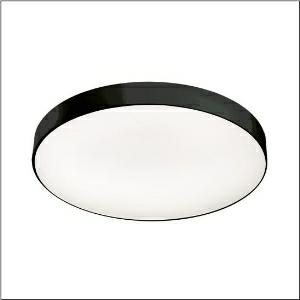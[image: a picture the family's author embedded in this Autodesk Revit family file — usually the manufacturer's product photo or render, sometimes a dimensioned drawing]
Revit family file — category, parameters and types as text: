
# Revit family: round_21_l_51mr38nd0421b
name_source: partatom
category: Lighting Fixtures
units: mm (PartAtom-declared; Revit-internal decimal feet)

## family parameters
Cut with Voids When Loaded = No
Host = Face
Light Source = No
Part Type = Normal
Room Calculation Point = No
Round Connector Dimension = Use Diameter
Shared = No

## types (1)
- Round 21 L (1 x LED, 12230 lm, 88.2 W, 4000K)
    Apparent Load = 88 VA
    CIE Flux Codes = 66 90 98 71 100
    Color Rendering = 80
    Color Temperature = 4000K
    Default Elevation = 1800 mm
    Description = Round 21 L, wall and ceiling luminaire, primary optical cover: micro prismatic cover, of PMMA, transparent, CAT 2 (L<= 3000cd/m²), light emission: direct/indirect distribution, primary light characteristic: symmetric, installation type: suspended mounting, surface-mounted, LED, rated luminous flux: 12.230lm, luminous efficacy: 139lm/W, light colour: 840, colour temperature: 4000K, control gear: DALI 2, with terminal, 5-pole, mains connection: 230V, AC, 50/60Hz, rated input power: 88W, housing, of aluminium, coated, black, diameter: 850mm, height: 62mm, protection rating (complete): IP40, insulation class (complete): insulation class I (protective earthing), certification: CE, impact resistance: IK04, permissible operating ambient temperature: -10..+35°C, packaging unit: 1 piece
    Height = 87 mm
    Lamp = 1 x LED
    Lamp Light Flux = 12230 lm
    Lamp Power = 88.2 W
    Lamp count = 1
    Length = 850 mm
    Luminous efficacy = 139 lm/W
    Manufacturer = Siteco
    ModVariant = No
    Model = 51MR38ND0421B
    Mounting Place = Ceiling
    Mounting Type = Surface mounted
    Number of Poles = 1
    OnlyDefault = Yes
    Power Factor = 1
    Product Name = Round 21 L
    Product group = wall and ceiling luminaire
    ProductGroupID = 304
    Protection Class = Protection class I
    Protection Degree = IP 40
    RLX_Detail_Level = 1
    RLX_Emergency_Light_Flux = 0 lm
    RLX_Emergency_Type = 0
    RLX_Emergency_Type_DB = No
    RlxData = <blob elided: 28709 chars, md5=83ed1eae>
    Socket = socket
    Standby Power = 0 W
    System Light Flux = 12230 lm
    System Power = 88 W
    Type Comments = Product without accessories
    Type Image = l_1258326.jpg
    URL = http://relux.com
    VarID = ---
    Voltage = 0 V
    Weight = 0.00 kg
    Width = 0 mm  [stored 0 ft]

note: [stored X ft] marks values corroborated as IEEE doubles in the binary element streams (Revit-internal decimal feet)

## geometry (parser evidence)
native form markers: Blend x4, Sweep x11
no freeform markers — native parametric forms only
